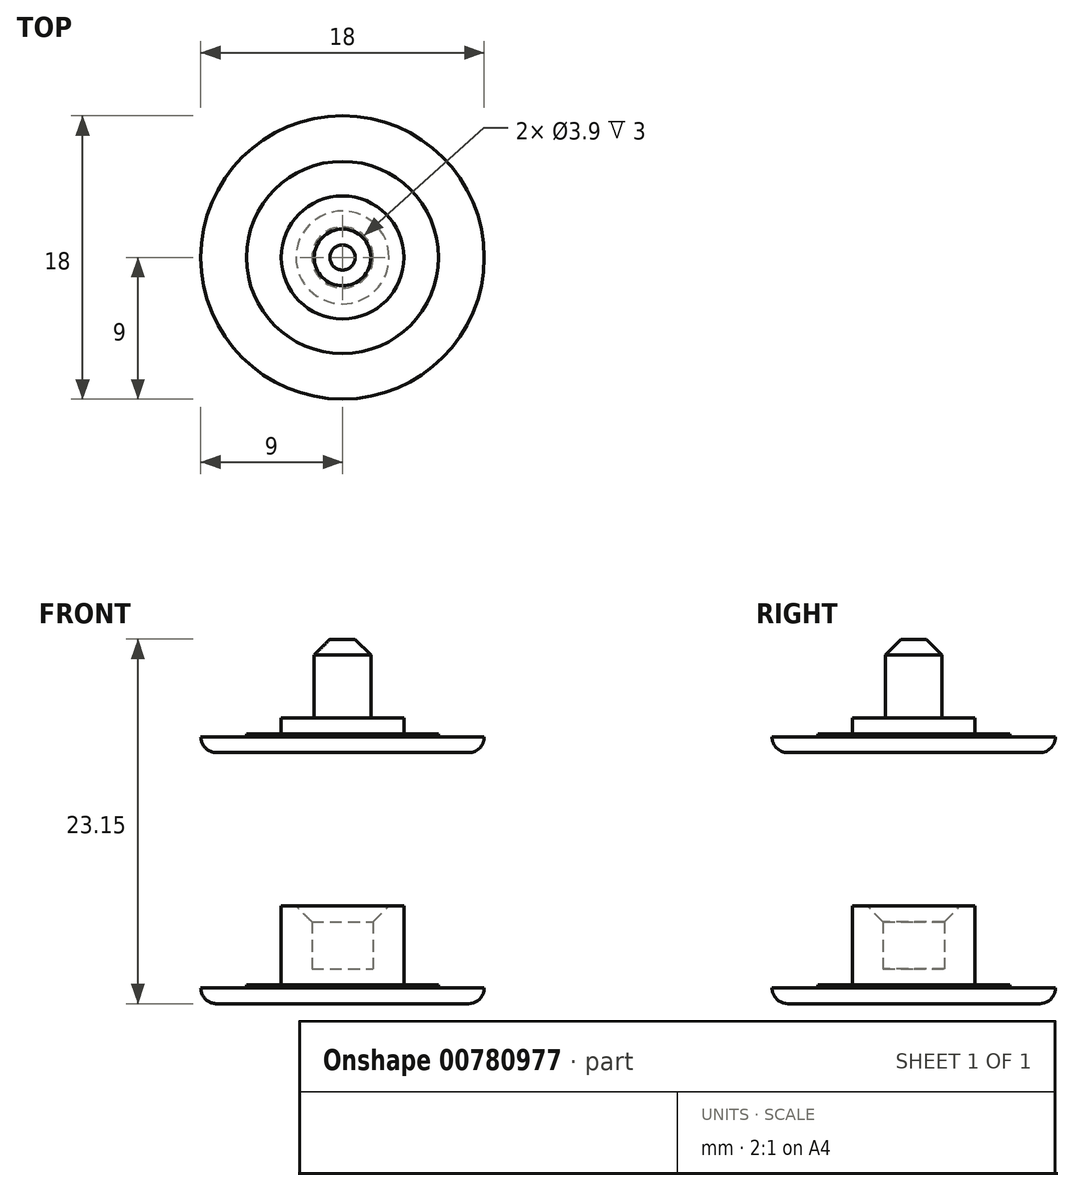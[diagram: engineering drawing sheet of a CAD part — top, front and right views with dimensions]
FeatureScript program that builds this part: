
annotation { "Feature Type Name" : "Feature", "Feature Type Description" : "" }
export const myFeature = defineFeature(function(context is Context, id is Id, definition is map)
    precondition{}
    {
        {
            var Q0;
            Q0=qCreatedBy(makeId("Front.planeOp"),FACE);
            var sketch = newSketch(context, id + "F0", { "sketchPlane" : qUnion([Q0])});
            skLineSegment(sketch, "E0.bottom", {"start": v(0, 0) * mm, "end": v(9, 0) * mm});
            skLineSegment(sketch, "E0.top", {"start": v(6.1, 1) * mm, "end": v(9, 1) * mm});
            skLineSegment(sketch, "E0.left", {"start": v(0, 0) * mm, "end": v(0, 1) * mm});
            skLineSegment(sketch, "E0.right", {"start": v(9, 0) * mm, "end": v(9, 1) * mm});
            skLineSegment(sketch, "E1.left", {"start": v(0, 1) * mm, "end": v(0, 1.7) * mm});
            skLineSegment(sketch, "E1.right", {"start": v(6.1, 1) * mm, "end": v(6.1, 1.2) * mm});
            skLineSegment(sketch, "E2.top", {"start": v(1.95, 6.2) * mm, "end": v(3.9, 6.2) * mm});
            skLineSegment(sketch, "E2.left", {"start": v(0, 1.7) * mm, "end": v(0, 2.2) * mm});
            skLineSegment(sketch, "E2.right", {"start": v(3.9, 1.2) * mm, "end": v(3.9, 6.2) * mm});
            skLineSegment(sketch, "E3.top", {"start": v(0, 2.2) * mm, "end": v(1.95, 2.2) * mm});
            skLineSegment(sketch, "E3.right", {"start": v(1.95, 6.2) * mm, "end": v(1.95, 2.2) * mm});
            skLineSegment(sketch, "E4.trimOffspring", {"start": v(3.9, 1.2) * mm, "end": v(6.1, 1.2) * mm});
            skSolve(sketch);
        }
        {
            var Q0;
            Q0=makeQuery(id+"F0.imprint","IMPRINT",FACE,{"disambiguationData":[TD([[makeQuery(id+"F0.imprint","IMPRINT",EDGE,{"derivedFrom":sQuery(id+"F0.wireOp",EDGE,"E0.bottom")}),1.0]])]});
            var Q1;
            Q1=sQuery(id+"F0.wireOp",EDGE,"E2.left");
            revolve(context, id + "F1", {"surfaceOperationType" : NewSurfaceOperationType.NEW, "entities" : qUnion([Q0]), "axis" : qUnion([Q1]), "revolveType" : RevolveType.FULL});
        }
        {
            var Q0;
            Q0=makeQuery(id+"F1.opRevolve","SWEPT_EDGE",EDGE,{"disambiguationData":[OSD([sQuery(id+"F0.wireOp",EDGE,"E0.bottom"),sQuery(id+"F0.wireOp",EDGE,"E0.right")])]});
            fillet(context, id + "F2", {"entities" : qUnion([Q0]), "radius" : 1 * mm, "tangentPropagation" : true, "allowEdgeOverflow" : false});
        }
        {
            var Q0;
            Q0=makeQuery(id+"F1.opRevolve","SWEPT_EDGE",EDGE,{"disambiguationData":[OSD([sQuery(id+"F0.wireOp",EDGE,"E2.top"),sQuery(id+"F0.wireOp",EDGE,"E3.right")])]});
            chamfer(context, id + "F3", {"entities" : qUnion([Q0]), "width" : 1 * mm, "tangentPropagation" : true});
        }
        {
            var Q0;
            Q0=qCreatedBy(makeId("Front.planeOp"),FACE);
            var sketch = newSketch(context, id + "F4", { "sketchPlane" : qUnion([Q0])});
            skLineSegment(sketch, "E5.bottom", {"start": v(0, 15.95) * mm, "end": v(9, 15.95) * mm});
            skLineSegment(sketch, "E5.top", {"start": v(6.1, 16.95) * mm, "end": v(9, 16.95) * mm});
            skLineSegment(sketch, "E5.left", {"start": v(0, 15.95) * mm, "end": v(0, 16.95) * mm});
            skLineSegment(sketch, "E5.right", {"start": v(9, 15.95) * mm, "end": v(9, 16.95) * mm});
            skLineSegment(sketch, "E6.top", {"start": v(3.9, 17.15) * mm, "end": v(6.1, 17.15) * mm});
            skLineSegment(sketch, "E6.left", {"start": v(0, 16.95) * mm, "end": v(0, 17.15) * mm});
            skLineSegment(sketch, "E6.right", {"start": v(6.1, 16.95) * mm, "end": v(6.1, 17.15) * mm});
            skLineSegment(sketch, "E7.top", {"start": v(1.8, 18.15) * mm, "end": v(3.9, 18.15) * mm});
            skLineSegment(sketch, "E7.left", {"start": v(0, 17.15) * mm, "end": v(0, 18.15) * mm});
            skLineSegment(sketch, "E7.right", {"start": v(3.9, 17.15) * mm, "end": v(3.9, 18.15) * mm});
            skLineSegment(sketch, "E8.top", {"start": v(0, 23.15) * mm, "end": v(1.8, 23.15) * mm});
            skLineSegment(sketch, "E8.left", {"start": v(0, 18.15) * mm, "end": v(0, 23.15) * mm});
            skLineSegment(sketch, "E8.right", {"start": v(1.8, 18.15) * mm, "end": v(1.8, 23.15) * mm});
            skSolve(sketch);
        }
        {
            var Q0;
            Q0=makeQuery(id+"F4.imprint","IMPRINT",FACE,{"disambiguationData":[TD([[makeQuery(id+"F4.imprint","IMPRINT",EDGE,{"derivedFrom":sQuery(id+"F4.wireOp",EDGE,"E5.bottom")}),1.0]])]});
            var Q1;
            Q1=sQuery(id+"F4.wireOp",EDGE,"E7.left");
            revolve(context, id + "F5", {"surfaceOperationType" : NewSurfaceOperationType.NEW, "entities" : qUnion([Q0]), "axis" : qUnion([Q1]), "revolveType" : RevolveType.FULL});
        }
        {
            var Q0;
            Q0=makeQuery(id+"F5.opRevolve","SWEPT_EDGE",EDGE,{"disambiguationData":[OSD([sQuery(id+"F4.wireOp",EDGE,"E5.bottom"),sQuery(id+"F4.wireOp",EDGE,"E5.right")])]});
            fillet(context, id + "F6", {"entities" : qUnion([Q0]), "radius" : 1 * mm, "tangentPropagation" : true, "allowEdgeOverflow" : false});
        }
        {
            var Q0;
            Q0=makeQuery(id+"F5.opRevolve","SWEPT_EDGE",EDGE,{"disambiguationData":[OSD([sQuery(id+"F4.wireOp",EDGE,"E8.top"),sQuery(id+"F4.wireOp",EDGE,"E8.right")])]});
            chamfer(context, id + "F7", {"entities" : qUnion([Q0]), "width" : 1 * mm, "tangentPropagation" : true});
        }
    });
